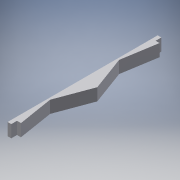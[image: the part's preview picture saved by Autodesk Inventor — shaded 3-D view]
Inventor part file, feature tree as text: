
AUTODESK INVENTOR PART (.ipt)
format: ipt  version: 2017 (Build 210142000, 142)  size: 122,880 bytes
history: native  units: in
note: dims shown in document units (in); Inventor stores cm internally (conversion verified against a paired STEP export)
features: extrude x3, sketch x3
ambient origin geometry x8: Origin, YZ Plane, XZ Plane, XY Plane, X Axis, Y Axis, Z Axis, Center Point
bodies: Solid1 (feature_tree)
feature tree (6):
  extrude  "Extrusion1"  Depth=0.134in
  sketch  "Sketch2"  dims[d2=0.134in d3=0.612in]
  extrude  "Extrusion2"  Depth=0.134in
  extrude  "Extrusion3"  Depth=0.065in
  sketch  "Sketch1"  dims[d0=2.436in d1=0.134in]
  sketch  "Sketch3"  dims[d4=1.223in d5=0.612in d6=0.035in d7=0.035in d8=0.2875in d9=0.0in d10=0.259in d12=0.065in d13=0.101in d14=0.0in d15=0.101in d16=0.0in d17=0.065in]
